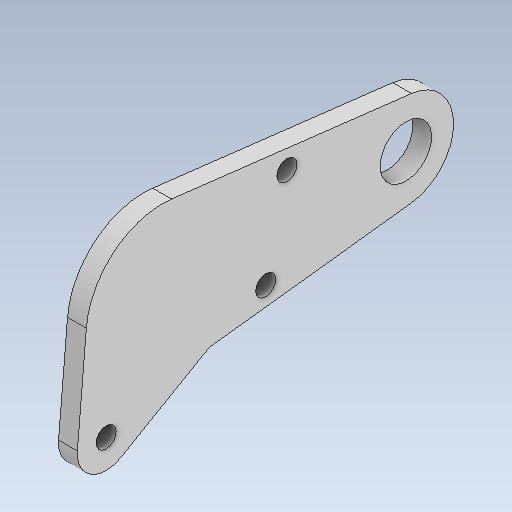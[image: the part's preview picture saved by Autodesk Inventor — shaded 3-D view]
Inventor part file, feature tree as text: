
AUTODESK INVENTOR PART (.ipt)
format: ipt  version: 2020 (Build 240168000, 168)  size: 228,864 bytes
history: native  units: mm
features: extrude x5, sketch x4, projected_geometry x3
ambient origin geometry x8: Origin, YZ Plane, XZ Plane, XY Plane, X Axis, Y Axis, Z Axis, Center Point
bodies: Body1 (feature_tree)
feature tree (12):
  extrude  "Выдавливание4"  Depth=18.6mm
  extrude  "Выдавливание5"  Depth=12.2mm
  extrude  "Выдавливание6"  Depth=9.7mm
  extrude  "Выдавливание7"  Depth=7.1mm
  extrude  "Выдавливание8"  Depth=38.82013mm
  sketch  "Эскиз4"
  projected_geometry  "Спроецированная петля3"
  sketch  "Эскиз5"
  sketch  "Эскиз6"
  projected_geometry  "Спроецированная петля4"
  sketch  "Эскиз7"
  projected_geometry  "Спроецированная петля5"
